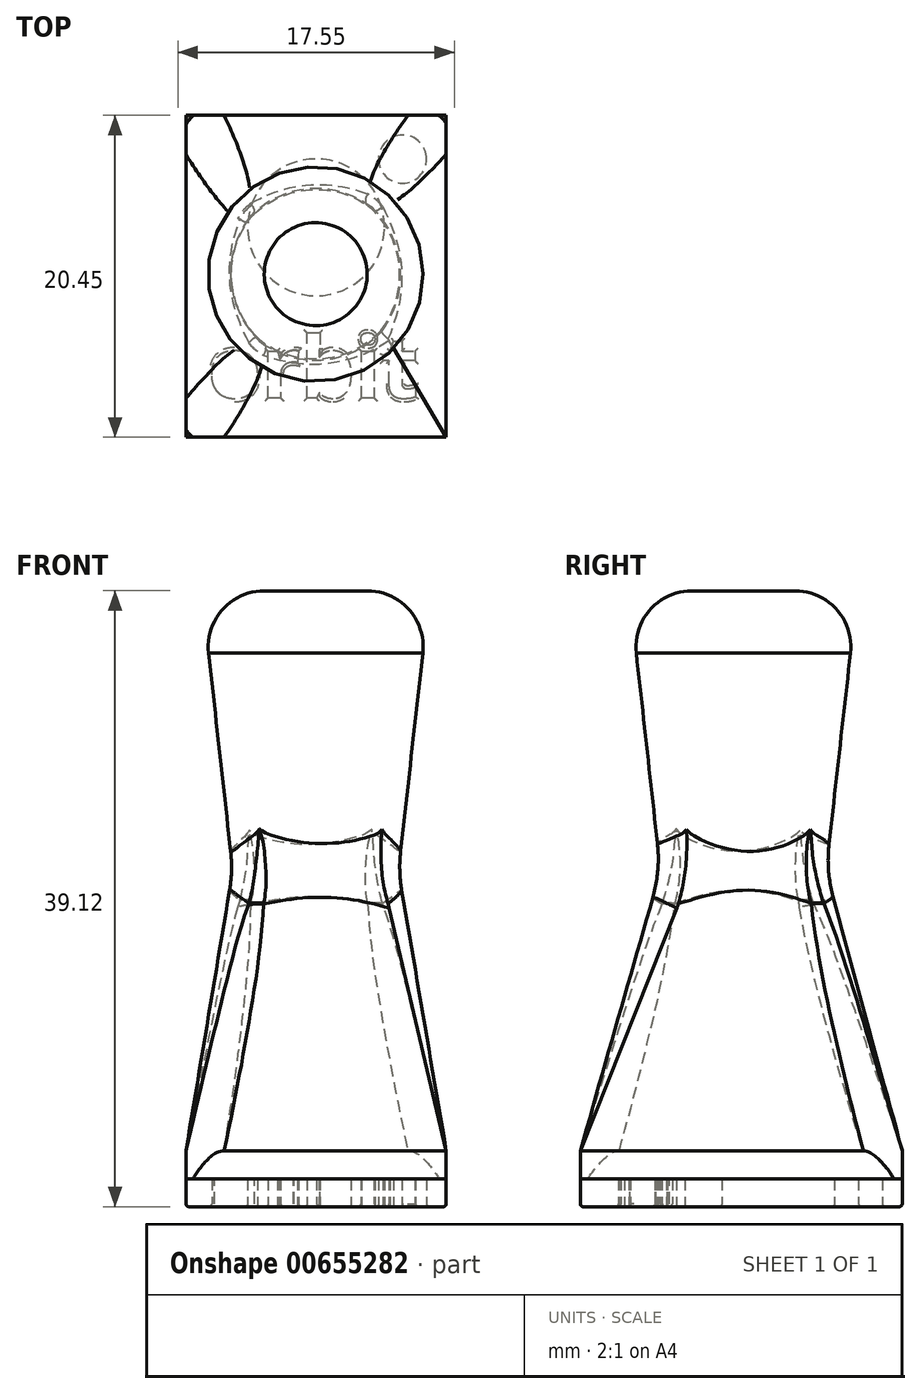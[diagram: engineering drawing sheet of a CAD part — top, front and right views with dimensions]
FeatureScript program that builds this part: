
annotation { "Feature Type Name" : "Feature", "Feature Type Description" : "" }
export const myFeature = defineFeature(function(context is Context, id is Id, definition is map)
    precondition{}
    {
        {
            var Q0;
            Q0=qCreatedBy(makeId("Top.planeOp"),FACE);
            var sketch = newSketch(context, id + "F0", { "sketchPlane" : qUnion([Q0])});
            skCircle(sketch, "E0", {"center": v(2.63, -1.24) * mm, "radius": 6.21 * mm});
            skLineSegment(sketch, "E1.bottom", {"start": v(-9.17, -20.29) * mm, "end": v(14.44, -20.29) * mm});
            skLineSegment(sketch, "E1.top", {"start": v(-9.17, 8.92) * mm, "end": v(14.44, 8.92) * mm});
            skLineSegment(sketch, "E1.left", {"start": v(-9.17, -20.29) * mm, "end": v(-9.17, 8.92) * mm});
            skLineSegment(sketch, "E1.right", {"start": v(14.44, -20.29) * mm, "end": v(14.44, 8.92) * mm});
            skPoint(sketch, "E1.middle", {"position": v(2.63, -5.68) * mm});
            skText(sketch, "E2", { "text": "orbit", "fontName": "OpenSans-Bold.ttf"});
            skCircle(sketch, "E3", {"center": v(10.48, 4.96) * mm, "radius": 2.18 * mm});
            const initialGuessF0  = {"E2": [-0.00718, -0.01673, 1, 0, 0.00562]};
            skSetInitialGuess(sketch, initialGuessF0);
            skSolve(sketch);
        }
        {
            var Q0;
            Q0=makeQuery(id+"F0.imprint","IMPRINT",FACE,{"disambiguationData":[TD([[makeQuery(id+"F0.imprint","IMPRINT",EDGE,{"derivedFrom":sQuery(id+"F0.wireOp",EDGE,"E0")}),-1.0]])]});
            var Q1;
            Q1=makeQuery(id+"F0.imprint","IMPRINT",FACE,{"disambiguationData":[TD([[makeQuery(id+"F0.imprint","IMPRINT",EDGE,{"derivedFrom":sQuery(id+"F0.wireOp",EDGE,"6c242687-06e7-4fa3-8755-0ec345e10ca5.sketch_text.stroke-45")}),1.0]])]});
            var Q2;
            Q2=makeQuery(id+"F0.imprint","IMPRINT",FACE,{"disambiguationData":[TD([[makeQuery(id+"F0.imprint","IMPRINT",EDGE,{"derivedFrom":sQuery(id+"F0.wireOp",EDGE,"6c242687-06e7-4fa3-8755-0ec345e10ca5.sketch_text.stroke-9")}),1.0]])]});
            extrude(context, id + "F1", {"entities" : qUnion([Q0, Q1, Q2]), "depth" : 2.54 * mm, "offsetDistance" : 25.4 * mm});
        }
        {
            var Q0;
            Q0=makeQuery(id+"F1.opExtrude","CAP_FACE",FACE,{"disambiguationData":[OSD([sQuery(id+"F0.wireOp",EDGE,"E0"),sQuery(id+"F0.wireOp",EDGE,"53a408db-f14d-4eee-ab72-fbaa9f21d148"),sQuery(id+"F0.wireOp",EDGE,"6c242687-06e7-4fa3-8755-0ec345e10ca5.sketch_text.stroke-0"),sQuery(id+"F0.wireOp",EDGE,"6c242687-06e7-4fa3-8755-0ec345e10ca5.sketch_text.stroke-1"),sQuery(id+"F0.wireOp",EDGE,"6c242687-06e7-4fa3-8755-0ec345e10ca5.sketch_text.stroke-2"),sQuery(id+"F0.wireOp",EDGE,"6c242687-06e7-4fa3-8755-0ec345e10ca5.sketch_text.stroke-3"),sQuery(id+"F0.wireOp",EDGE,"6c242687-06e7-4fa3-8755-0ec345e10ca5.sketch_text.stroke-4"),sQuery(id+"F0.wireOp",EDGE,"6c242687-06e7-4fa3-8755-0ec345e10ca5.sketch_text.stroke-5"),sQuery(id+"F0.wireOp",EDGE,"6c242687-06e7-4fa3-8755-0ec345e10ca5.sketch_text.stroke-6"),sQuery(id+"F0.wireOp",EDGE,"6c242687-06e7-4fa3-8755-0ec345e10ca5.sketch_text.stroke-7"),sQuery(id+"F0.wireOp",EDGE,"6c242687-06e7-4fa3-8755-0ec345e10ca5.sketch_text.stroke-8"),sQuery(id+"F0.wireOp",EDGE,"6c242687-06e7-4fa3-8755-0ec345e10ca5.sketch_text.stroke-17"),sQuery(id+"F0.wireOp",EDGE,"6c242687-06e7-4fa3-8755-0ec345e10ca5.sketch_text.stroke-18"),sQuery(id+"F0.wireOp",EDGE,"6c242687-06e7-4fa3-8755-0ec345e10ca5.sketch_text.stroke-19"),sQuery(id+"F0.wireOp",EDGE,"6c242687-06e7-4fa3-8755-0ec345e10ca5.sketch_text.stroke-20"),sQuery(id+"F0.wireOp",EDGE,"6c242687-06e7-4fa3-8755-0ec345e10ca5.sketch_text.stroke-21"),sQuery(id+"F0.wireOp",EDGE,"6c242687-06e7-4fa3-8755-0ec345e10ca5.sketch_text.stroke-22"),sQuery(id+"F0.wireOp",EDGE,"6c242687-06e7-4fa3-8755-0ec345e10ca5.sketch_text.stroke-23"),sQuery(id+"F0.wireOp",EDGE,"6c242687-06e7-4fa3-8755-0ec345e10ca5.sketch_text.stroke-24"),sQuery(id+"F0.wireOp",EDGE,"6c242687-06e7-4fa3-8755-0ec345e10ca5.sketch_text.stroke-25"),sQuery(id+"F0.wireOp",EDGE,"6c242687-06e7-4fa3-8755-0ec345e10ca5.sketch_text.stroke-26"),sQuery(id+"F0.wireOp",EDGE,"6c242687-06e7-4fa3-8755-0ec345e10ca5.sketch_text.stroke-27"),sQuery(id+"F0.wireOp",EDGE,"6c242687-06e7-4fa3-8755-0ec345e10ca5.sketch_text.stroke-28"),sQuery(id+"F0.wireOp",EDGE,"6c242687-06e7-4fa3-8755-0ec345e10ca5.sketch_text.stroke-29"),sQuery(id+"F0.wireOp",EDGE,"6c242687-06e7-4fa3-8755-0ec345e10ca5.sketch_text.stroke-30"),sQuery(id+"F0.wireOp",EDGE,"6c242687-06e7-4fa3-8755-0ec345e10ca5.sketch_text.stroke-31"),sQuery(id+"F0.wireOp",EDGE,"6c242687-06e7-4fa3-8755-0ec345e10ca5.sketch_text.stroke-32"),sQuery(id+"F0.wireOp",EDGE,"6c242687-06e7-4fa3-8755-0ec345e10ca5.sketch_text.stroke-33"),sQuery(id+"F0.wireOp",EDGE,"6c242687-06e7-4fa3-8755-0ec345e10ca5.sketch_text.stroke-34"),sQuery(id+"F0.wireOp",EDGE,"6c242687-06e7-4fa3-8755-0ec345e10ca5.sketch_text.stroke-35"),sQuery(id+"F0.wireOp",EDGE,"6c242687-06e7-4fa3-8755-0ec345e10ca5.sketch_text.stroke-36"),sQuery(id+"F0.wireOp",EDGE,"6c242687-06e7-4fa3-8755-0ec345e10ca5.sketch_text.stroke-37"),sQuery(id+"F0.wireOp",EDGE,"6c242687-06e7-4fa3-8755-0ec345e10ca5.sketch_text.stroke-38"),sQuery(id+"F0.wireOp",EDGE,"6c242687-06e7-4fa3-8755-0ec345e10ca5.sketch_text.stroke-39"),sQuery(id+"F0.wireOp",EDGE,"6c242687-06e7-4fa3-8755-0ec345e10ca5.sketch_text.stroke-40"),sQuery(id+"F0.wireOp",EDGE,"6c242687-06e7-4fa3-8755-0ec345e10ca5.sketch_text.stroke-41"),sQuery(id+"F0.wireOp",EDGE,"6c242687-06e7-4fa3-8755-0ec345e10ca5.sketch_text.stroke-42"),sQuery(id+"F0.wireOp",EDGE,"6c242687-06e7-4fa3-8755-0ec345e10ca5.sketch_text.stroke-43"),sQuery(id+"F0.wireOp",EDGE,"6c242687-06e7-4fa3-8755-0ec345e10ca5.sketch_text.stroke-44"),sQuery(id+"F0.wireOp",EDGE,"6c242687-06e7-4fa3-8755-0ec345e10ca5.sketch_text.stroke-53"),sQuery(id+"F0.wireOp",EDGE,"6c242687-06e7-4fa3-8755-0ec345e10ca5.sketch_text.stroke-54"),sQuery(id+"F0.wireOp",EDGE,"6c242687-06e7-4fa3-8755-0ec345e10ca5.sketch_text.stroke-55"),sQuery(id+"F0.wireOp",EDGE,"6c242687-06e7-4fa3-8755-0ec345e10ca5.sketch_text.stroke-56"),sQuery(id+"F0.wireOp",EDGE,"6c242687-06e7-4fa3-8755-0ec345e10ca5.sketch_text.stroke-57"),sQuery(id+"F0.wireOp",EDGE,"6c242687-06e7-4fa3-8755-0ec345e10ca5.sketch_text.stroke-58"),sQuery(id+"F0.wireOp",EDGE,"6c242687-06e7-4fa3-8755-0ec345e10ca5.sketch_text.stroke-59"),sQuery(id+"F0.wireOp",EDGE,"6c242687-06e7-4fa3-8755-0ec345e10ca5.sketch_text.stroke-60"),sQuery(id+"F0.wireOp",EDGE,"6c242687-06e7-4fa3-8755-0ec345e10ca5.sketch_text.stroke-61"),sQuery(id+"F0.wireOp",EDGE,"6c242687-06e7-4fa3-8755-0ec345e10ca5.sketch_text.stroke-62"),sQuery(id+"F0.wireOp",EDGE,"6c242687-06e7-4fa3-8755-0ec345e10ca5.sketch_text.stroke-63"),sQuery(id+"F0.wireOp",EDGE,"6c242687-06e7-4fa3-8755-0ec345e10ca5.sketch_text.stroke-64"),sQuery(id+"F0.wireOp",EDGE,"6c242687-06e7-4fa3-8755-0ec345e10ca5.sketch_text.stroke-65"),sQuery(id+"F0.wireOp",EDGE,"6c242687-06e7-4fa3-8755-0ec345e10ca5.sketch_text.stroke-66"),sQuery(id+"F0.wireOp",EDGE,"6c242687-06e7-4fa3-8755-0ec345e10ca5.sketch_text.stroke-67"),sQuery(id+"F0.wireOp",EDGE,"6c242687-06e7-4fa3-8755-0ec345e10ca5.sketch_text.stroke-68"),sQuery(id+"F0.wireOp",EDGE,"6c242687-06e7-4fa3-8755-0ec345e10ca5.sketch_text.stroke-69"),sQuery(id+"F0.wireOp",EDGE,"6c242687-06e7-4fa3-8755-0ec345e10ca5.sketch_text.stroke-70"),sQuery(id+"F0.wireOp",EDGE,"6c242687-06e7-4fa3-8755-0ec345e10ca5.sketch_text.stroke-71"),sQuery(id+"F0.wireOp",EDGE,"6c242687-06e7-4fa3-8755-0ec345e10ca5.sketch_text.stroke-72"),sQuery(id+"F0.wireOp",EDGE,"6c242687-06e7-4fa3-8755-0ec345e10ca5.sketch_text.stroke-73"),sQuery(id+"F0.wireOp",EDGE,"6c242687-06e7-4fa3-8755-0ec345e10ca5.sketch_text.stroke-74"),sQuery(id+"F0.wireOp",EDGE,"6c242687-06e7-4fa3-8755-0ec345e10ca5.sketch_text.stroke-75"),sQuery(id+"F0.wireOp",EDGE,"6c242687-06e7-4fa3-8755-0ec345e10ca5.sketch_text.stroke-76"),sQuery(id+"F0.wireOp",EDGE,"6c242687-06e7-4fa3-8755-0ec345e10ca5.sketch_text.stroke-77"),sQuery(id+"F0.wireOp",EDGE,"6c242687-06e7-4fa3-8755-0ec345e10ca5.sketch_text.stroke-78"),sQuery(id+"F0.wireOp",EDGE,"6c242687-06e7-4fa3-8755-0ec345e10ca5.sketch_text.stroke-79"),sQuery(id+"F0.wireOp",EDGE,"6c242687-06e7-4fa3-8755-0ec345e10ca5.sketch_text.stroke-80"),sQuery(id+"F0.wireOp",EDGE,"6c242687-06e7-4fa3-8755-0ec345e10ca5.sketch_text.stroke-81"),sQuery(id+"F0.wireOp",EDGE,"6c242687-06e7-4fa3-8755-0ec345e10ca5.sketch_text.stroke-82"),sQuery(id+"F0.wireOp",EDGE,"6c242687-06e7-4fa3-8755-0ec345e10ca5.sketch_text.stroke-83"),sQuery(id+"F0.wireOp",EDGE,"E1.bottom"),sQuery(id+"F0.wireOp",EDGE,"E1.top"),sQuery(id+"F0.wireOp",EDGE,"E1.left"),sQuery(id+"F0.wireOp",EDGE,"E1.right")])],"isStart":false});
            var sketch = newSketch(context, id + "F2", { "sketchPlane" : qUnion([Q0])});
            skLineSegment(sketch, "E4.bottom", {"start": v(14.44, -20.29) * mm, "end": v(-9.17, -20.29) * mm});
            skLineSegment(sketch, "E4.top", {"start": v(14.44, 8.92) * mm, "end": v(-9.17, 8.92) * mm});
            skLineSegment(sketch, "E4.left", {"start": v(14.44, -20.29) * mm, "end": v(14.44, 8.92) * mm});
            skLineSegment(sketch, "E4.right", {"start": v(-9.17, -20.29) * mm, "end": v(-9.17, 8.92) * mm});
            skSolve(sketch);
        }
        {
            var Q0;
            Q0 = qSketchRegion(id + "F2", true);
            extrude(context, id + "F3", {"entities" : qUnion([Q0]), "depth" : 2.54 * mm, "offsetDistance" : 25.4 * mm});
        }
        {
            var Q0;
            Q0=makeQuery(id+"F1.opExtrude","CAP_EDGE",EDGE,{"disambiguationData":[OSD([sQuery(id+"F0.wireOp",EDGE,"E0")])],"isStart":true});
            var Q1;
            Q1=makeQuery(id+"F1.opExtrude","CAP_EDGE",EDGE,{"disambiguationData":[OSD([sQuery(id+"F0.wireOp",EDGE,"53a408db-f14d-4eee-ab72-fbaa9f21d148")])],"isStart":true});
            fillet(context, id + "F4", {"entities" : qUnion([Q0, Q1]), "radius" : 0.25 * mm, "tangentPropagation" : true, "allowEdgeOverflow" : false});
        }
        {
            var Q0;
            Q0=makeQuery(id+"F1.opExtrude","CAP_FACE",FACE,{"disambiguationData":[OSD([sQuery(id+"F0.wireOp",EDGE,"E0"),sQuery(id+"F0.wireOp",EDGE,"53a408db-f14d-4eee-ab72-fbaa9f21d148"),sQuery(id+"F0.wireOp",EDGE,"6c242687-06e7-4fa3-8755-0ec345e10ca5.sketch_text.stroke-0"),sQuery(id+"F0.wireOp",EDGE,"6c242687-06e7-4fa3-8755-0ec345e10ca5.sketch_text.stroke-1"),sQuery(id+"F0.wireOp",EDGE,"6c242687-06e7-4fa3-8755-0ec345e10ca5.sketch_text.stroke-2"),sQuery(id+"F0.wireOp",EDGE,"6c242687-06e7-4fa3-8755-0ec345e10ca5.sketch_text.stroke-3"),sQuery(id+"F0.wireOp",EDGE,"6c242687-06e7-4fa3-8755-0ec345e10ca5.sketch_text.stroke-4"),sQuery(id+"F0.wireOp",EDGE,"6c242687-06e7-4fa3-8755-0ec345e10ca5.sketch_text.stroke-5"),sQuery(id+"F0.wireOp",EDGE,"6c242687-06e7-4fa3-8755-0ec345e10ca5.sketch_text.stroke-6"),sQuery(id+"F0.wireOp",EDGE,"6c242687-06e7-4fa3-8755-0ec345e10ca5.sketch_text.stroke-7"),sQuery(id+"F0.wireOp",EDGE,"6c242687-06e7-4fa3-8755-0ec345e10ca5.sketch_text.stroke-8"),sQuery(id+"F0.wireOp",EDGE,"6c242687-06e7-4fa3-8755-0ec345e10ca5.sketch_text.stroke-17"),sQuery(id+"F0.wireOp",EDGE,"6c242687-06e7-4fa3-8755-0ec345e10ca5.sketch_text.stroke-18"),sQuery(id+"F0.wireOp",EDGE,"6c242687-06e7-4fa3-8755-0ec345e10ca5.sketch_text.stroke-19"),sQuery(id+"F0.wireOp",EDGE,"6c242687-06e7-4fa3-8755-0ec345e10ca5.sketch_text.stroke-20"),sQuery(id+"F0.wireOp",EDGE,"6c242687-06e7-4fa3-8755-0ec345e10ca5.sketch_text.stroke-21"),sQuery(id+"F0.wireOp",EDGE,"6c242687-06e7-4fa3-8755-0ec345e10ca5.sketch_text.stroke-22"),sQuery(id+"F0.wireOp",EDGE,"6c242687-06e7-4fa3-8755-0ec345e10ca5.sketch_text.stroke-23"),sQuery(id+"F0.wireOp",EDGE,"6c242687-06e7-4fa3-8755-0ec345e10ca5.sketch_text.stroke-24"),sQuery(id+"F0.wireOp",EDGE,"6c242687-06e7-4fa3-8755-0ec345e10ca5.sketch_text.stroke-25"),sQuery(id+"F0.wireOp",EDGE,"6c242687-06e7-4fa3-8755-0ec345e10ca5.sketch_text.stroke-26"),sQuery(id+"F0.wireOp",EDGE,"6c242687-06e7-4fa3-8755-0ec345e10ca5.sketch_text.stroke-27"),sQuery(id+"F0.wireOp",EDGE,"6c242687-06e7-4fa3-8755-0ec345e10ca5.sketch_text.stroke-28"),sQuery(id+"F0.wireOp",EDGE,"6c242687-06e7-4fa3-8755-0ec345e10ca5.sketch_text.stroke-29"),sQuery(id+"F0.wireOp",EDGE,"6c242687-06e7-4fa3-8755-0ec345e10ca5.sketch_text.stroke-30"),sQuery(id+"F0.wireOp",EDGE,"6c242687-06e7-4fa3-8755-0ec345e10ca5.sketch_text.stroke-31"),sQuery(id+"F0.wireOp",EDGE,"6c242687-06e7-4fa3-8755-0ec345e10ca5.sketch_text.stroke-32"),sQuery(id+"F0.wireOp",EDGE,"6c242687-06e7-4fa3-8755-0ec345e10ca5.sketch_text.stroke-33"),sQuery(id+"F0.wireOp",EDGE,"6c242687-06e7-4fa3-8755-0ec345e10ca5.sketch_text.stroke-34"),sQuery(id+"F0.wireOp",EDGE,"6c242687-06e7-4fa3-8755-0ec345e10ca5.sketch_text.stroke-35"),sQuery(id+"F0.wireOp",EDGE,"6c242687-06e7-4fa3-8755-0ec345e10ca5.sketch_text.stroke-36"),sQuery(id+"F0.wireOp",EDGE,"6c242687-06e7-4fa3-8755-0ec345e10ca5.sketch_text.stroke-37"),sQuery(id+"F0.wireOp",EDGE,"6c242687-06e7-4fa3-8755-0ec345e10ca5.sketch_text.stroke-38"),sQuery(id+"F0.wireOp",EDGE,"6c242687-06e7-4fa3-8755-0ec345e10ca5.sketch_text.stroke-39"),sQuery(id+"F0.wireOp",EDGE,"6c242687-06e7-4fa3-8755-0ec345e10ca5.sketch_text.stroke-40"),sQuery(id+"F0.wireOp",EDGE,"6c242687-06e7-4fa3-8755-0ec345e10ca5.sketch_text.stroke-41"),sQuery(id+"F0.wireOp",EDGE,"6c242687-06e7-4fa3-8755-0ec345e10ca5.sketch_text.stroke-42"),sQuery(id+"F0.wireOp",EDGE,"6c242687-06e7-4fa3-8755-0ec345e10ca5.sketch_text.stroke-43"),sQuery(id+"F0.wireOp",EDGE,"6c242687-06e7-4fa3-8755-0ec345e10ca5.sketch_text.stroke-44"),sQuery(id+"F0.wireOp",EDGE,"6c242687-06e7-4fa3-8755-0ec345e10ca5.sketch_text.stroke-53"),sQuery(id+"F0.wireOp",EDGE,"6c242687-06e7-4fa3-8755-0ec345e10ca5.sketch_text.stroke-54"),sQuery(id+"F0.wireOp",EDGE,"6c242687-06e7-4fa3-8755-0ec345e10ca5.sketch_text.stroke-55"),sQuery(id+"F0.wireOp",EDGE,"6c242687-06e7-4fa3-8755-0ec345e10ca5.sketch_text.stroke-56"),sQuery(id+"F0.wireOp",EDGE,"6c242687-06e7-4fa3-8755-0ec345e10ca5.sketch_text.stroke-57"),sQuery(id+"F0.wireOp",EDGE,"6c242687-06e7-4fa3-8755-0ec345e10ca5.sketch_text.stroke-58"),sQuery(id+"F0.wireOp",EDGE,"6c242687-06e7-4fa3-8755-0ec345e10ca5.sketch_text.stroke-59"),sQuery(id+"F0.wireOp",EDGE,"6c242687-06e7-4fa3-8755-0ec345e10ca5.sketch_text.stroke-60"),sQuery(id+"F0.wireOp",EDGE,"6c242687-06e7-4fa3-8755-0ec345e10ca5.sketch_text.stroke-61"),sQuery(id+"F0.wireOp",EDGE,"6c242687-06e7-4fa3-8755-0ec345e10ca5.sketch_text.stroke-62"),sQuery(id+"F0.wireOp",EDGE,"6c242687-06e7-4fa3-8755-0ec345e10ca5.sketch_text.stroke-63"),sQuery(id+"F0.wireOp",EDGE,"6c242687-06e7-4fa3-8755-0ec345e10ca5.sketch_text.stroke-64"),sQuery(id+"F0.wireOp",EDGE,"6c242687-06e7-4fa3-8755-0ec345e10ca5.sketch_text.stroke-65"),sQuery(id+"F0.wireOp",EDGE,"6c242687-06e7-4fa3-8755-0ec345e10ca5.sketch_text.stroke-66"),sQuery(id+"F0.wireOp",EDGE,"6c242687-06e7-4fa3-8755-0ec345e10ca5.sketch_text.stroke-67"),sQuery(id+"F0.wireOp",EDGE,"6c242687-06e7-4fa3-8755-0ec345e10ca5.sketch_text.stroke-68"),sQuery(id+"F0.wireOp",EDGE,"6c242687-06e7-4fa3-8755-0ec345e10ca5.sketch_text.stroke-69"),sQuery(id+"F0.wireOp",EDGE,"6c242687-06e7-4fa3-8755-0ec345e10ca5.sketch_text.stroke-70"),sQuery(id+"F0.wireOp",EDGE,"6c242687-06e7-4fa3-8755-0ec345e10ca5.sketch_text.stroke-71"),sQuery(id+"F0.wireOp",EDGE,"6c242687-06e7-4fa3-8755-0ec345e10ca5.sketch_text.stroke-72"),sQuery(id+"F0.wireOp",EDGE,"6c242687-06e7-4fa3-8755-0ec345e10ca5.sketch_text.stroke-73"),sQuery(id+"F0.wireOp",EDGE,"6c242687-06e7-4fa3-8755-0ec345e10ca5.sketch_text.stroke-74"),sQuery(id+"F0.wireOp",EDGE,"6c242687-06e7-4fa3-8755-0ec345e10ca5.sketch_text.stroke-75"),sQuery(id+"F0.wireOp",EDGE,"6c242687-06e7-4fa3-8755-0ec345e10ca5.sketch_text.stroke-76"),sQuery(id+"F0.wireOp",EDGE,"6c242687-06e7-4fa3-8755-0ec345e10ca5.sketch_text.stroke-77"),sQuery(id+"F0.wireOp",EDGE,"6c242687-06e7-4fa3-8755-0ec345e10ca5.sketch_text.stroke-78"),sQuery(id+"F0.wireOp",EDGE,"6c242687-06e7-4fa3-8755-0ec345e10ca5.sketch_text.stroke-79"),sQuery(id+"F0.wireOp",EDGE,"6c242687-06e7-4fa3-8755-0ec345e10ca5.sketch_text.stroke-80"),sQuery(id+"F0.wireOp",EDGE,"6c242687-06e7-4fa3-8755-0ec345e10ca5.sketch_text.stroke-81"),sQuery(id+"F0.wireOp",EDGE,"6c242687-06e7-4fa3-8755-0ec345e10ca5.sketch_text.stroke-82"),sQuery(id+"F0.wireOp",EDGE,"6c242687-06e7-4fa3-8755-0ec345e10ca5.sketch_text.stroke-83"),sQuery(id+"F0.wireOp",EDGE,"E1.bottom"),sQuery(id+"F0.wireOp",EDGE,"E1.top"),sQuery(id+"F0.wireOp",EDGE,"E1.left"),sQuery(id+"F0.wireOp",EDGE,"E1.right")])],"isStart":true});
            var Q1;
            Q1=makeQuery(id+"F1.opExtrude","CAP_FACE",FACE,{"disambiguationData":[OSD([sQuery(id+"F0.wireOp",EDGE,"6c242687-06e7-4fa3-8755-0ec345e10ca5.sketch_text.stroke-45"),sQuery(id+"F0.wireOp",EDGE,"6c242687-06e7-4fa3-8755-0ec345e10ca5.sketch_text.stroke-46"),sQuery(id+"F0.wireOp",EDGE,"6c242687-06e7-4fa3-8755-0ec345e10ca5.sketch_text.stroke-47"),sQuery(id+"F0.wireOp",EDGE,"6c242687-06e7-4fa3-8755-0ec345e10ca5.sketch_text.stroke-48"),sQuery(id+"F0.wireOp",EDGE,"6c242687-06e7-4fa3-8755-0ec345e10ca5.sketch_text.stroke-49"),sQuery(id+"F0.wireOp",EDGE,"6c242687-06e7-4fa3-8755-0ec345e10ca5.sketch_text.stroke-50"),sQuery(id+"F0.wireOp",EDGE,"6c242687-06e7-4fa3-8755-0ec345e10ca5.sketch_text.stroke-51"),sQuery(id+"F0.wireOp",EDGE,"6c242687-06e7-4fa3-8755-0ec345e10ca5.sketch_text.stroke-52")])],"isStart":true});
            var Q2;
            Q2=makeQuery(id+"F1.opExtrude","CAP_FACE",FACE,{"disambiguationData":[OSD([sQuery(id+"F0.wireOp",EDGE,"6c242687-06e7-4fa3-8755-0ec345e10ca5.sketch_text.stroke-9"),sQuery(id+"F0.wireOp",EDGE,"6c242687-06e7-4fa3-8755-0ec345e10ca5.sketch_text.stroke-10"),sQuery(id+"F0.wireOp",EDGE,"6c242687-06e7-4fa3-8755-0ec345e10ca5.sketch_text.stroke-11"),sQuery(id+"F0.wireOp",EDGE,"6c242687-06e7-4fa3-8755-0ec345e10ca5.sketch_text.stroke-12"),sQuery(id+"F0.wireOp",EDGE,"6c242687-06e7-4fa3-8755-0ec345e10ca5.sketch_text.stroke-13"),sQuery(id+"F0.wireOp",EDGE,"6c242687-06e7-4fa3-8755-0ec345e10ca5.sketch_text.stroke-14"),sQuery(id+"F0.wireOp",EDGE,"6c242687-06e7-4fa3-8755-0ec345e10ca5.sketch_text.stroke-15"),sQuery(id+"F0.wireOp",EDGE,"6c242687-06e7-4fa3-8755-0ec345e10ca5.sketch_text.stroke-16")])],"isStart":true});
            fillet(context, id + "F5", {"entities" : qUnion([Q0, Q1, Q2]), "radius" : 0.25 * mm, "tangentPropagation" : true, "allowEdgeOverflow" : false});
        }
        {
            var Q0;
            Q0=makeQuery(id+"F3.opExtrude","CAP_FACE",FACE,{"disambiguationData":[OSD([sQuery(id+"F2.wireOp",EDGE,"E4.bottom"),sQuery(id+"F2.wireOp",EDGE,"E4.top"),sQuery(id+"F2.wireOp",EDGE,"E4.left"),sQuery(id+"F2.wireOp",EDGE,"E4.right")])],"isStart":false});
            cPlane(context, id + "F6", {"entities" : qUnion([Q0]), "cplaneType" : CPlaneType.OFFSET, "offset" : 25.4 * mm, "width" : 152.4 * mm, "height" : 152.4 * mm});
        }
        {
            var Q0;
            Q0=qCreatedBy(id+"F6.planeOp",FACE);
            var sketch = newSketch(context, id + "F7", { "sketchPlane" : qUnion([Q0])});
            skCircle(sketch, "E5", {"center": v(2.59, -5.5) * mm, "radius": 7.51 * mm});
            skSolve(sketch);
        }
        {
            var Q1;
            Q1=makeQuery(id+"F3.opExtrude","CAP_FACE",FACE,{"disambiguationData":[OSD([sQuery(id+"F2.wireOp",EDGE,"E4.bottom"),sQuery(id+"F2.wireOp",EDGE,"E4.top"),sQuery(id+"F2.wireOp",EDGE,"E4.left"),sQuery(id+"F2.wireOp",EDGE,"E4.right")])],"isStart":false});
            var Q2;
            Q2=makeQuery(id+"F7.imprint","IMPRINT",FACE,{"disambiguationData":[TD([[makeQuery(id+"F7.imprint","IMPRINT",EDGE,{"derivedFrom":sQuery(id+"F7.wireOp",EDGE,"E5")}),1.0]])]});
            loft(context, id + "F8", {"operationType" : NewBodyOperationType.ADD, "sheetProfilesArray" : [{ "sheetProfileEntities" : qUnion([Q1]) }, { "sheetProfileEntities" : qUnion([Q2]) }]});
        }
        {
            var Q0;
            Q0=makeQuery(id+"F8.opLoft","CAP_FACE",FACE,{"disambiguationData":[OSD([makeQuery(id+"F7.imprint","IMPRINT",FACE,{"disambiguationData":[TD([[makeQuery(id+"F7.imprint","IMPRINT",EDGE,{"derivedFrom":sQuery(id+"F7.wireOp",EDGE,"E5")}),1.0]])]})])],"isStart":true});
            cPlane(context, id + "F9", {"entities" : qUnion([Q0]), "cplaneType" : CPlaneType.OFFSET, "offset" : 25.4 * mm, "width" : 152.4 * mm, "height" : 152.4 * mm});
        }
        {
            var Q0;
            Q0=qCreatedBy(id+"F9.planeOp",FACE);
            var sketch = newSketch(context, id + "F10", { "sketchPlane" : qUnion([Q0])});
            skCircle(sketch, "E6", {"center": v(2.6, -5.48) * mm, "radius": 10.35 * mm});
            skSolve(sketch);
        }
        {
            var Q1;
            Q1=makeQuery(id+"F8.opLoft","CAP_FACE",FACE,{"disambiguationData":[OSD([makeQuery(id+"F7.imprint","IMPRINT",FACE,{"disambiguationData":[TD([[makeQuery(id+"F7.imprint","IMPRINT",EDGE,{"derivedFrom":sQuery(id+"F7.wireOp",EDGE,"E5")}),1.0]])]})])],"isStart":true});
            var Q2;
            Q2=makeQuery(id+"F10.imprint","IMPRINT",FACE,{"disambiguationData":[TD([[makeQuery(id+"F10.imprint","IMPRINT",EDGE,{"derivedFrom":sQuery(id+"F10.wireOp",EDGE,"E6")}),1.0]])]});
            loft(context, id + "F11", {"operationType" : NewBodyOperationType.ADD, "sheetProfilesArray" : [{ "sheetProfileEntities" : qUnion([Q1]) }, { "sheetProfileEntities" : qUnion([Q2]) }]});
        }
        {
            var Q0;
            {var subQ0=sQuery(id+"F7.wireOp",EDGE,"E5");var subQ1=sQuery(id+"F2.wireOp",EDGE,"E4.right");var subQ2=sQuery(id+"F2.wireOp",EDGE,"E4.bottom");Q0=makeQuery(id+"F11.boolean.opBoolean","MERGE",EDGE,{"derivedFrom":[makeQuery(id+"F8.opLoft","MID_CAP_EDGE",EDGE,{"disambiguationData":[OSD([subQ2,subQ1,subQ0])],"capPos":1.0}),makeQuery(id+"F11.opLoft","MID_CAP_EDGE",EDGE,{"disambiguationData":[OSD([subQ2,subQ1,subQ0])],"capPos":0.0})]});}
            var Q1;
            {var subQ0=sQuery(id+"F7.wireOp",EDGE,"E5");var subQ1=sQuery(id+"F2.wireOp",EDGE,"E4.right");var subQ2=sQuery(id+"F2.wireOp",EDGE,"E4.left");var subQ3=sQuery(id+"F2.wireOp",EDGE,"E4.top");var subQ4=sQuery(id+"F2.wireOp",EDGE,"E4.bottom");Q1=makeQuery(id+"F11.boolean.opBoolean","MERGE",EDGE,{"derivedFrom":[makeQuery(id+"F8.opLoft","MID_CAP_EDGE",EDGE,{"disambiguationData":[OSD([subQ4,subQ3,subQ2,subQ1,subQ0])],"capPos":1.0}),makeQuery(id+"F11.opLoft","MID_CAP_EDGE",EDGE,{"disambiguationData":[OSD([subQ4,subQ3,subQ2,subQ1,subQ0])],"capPos":0.0})]});}
            var Q2;
            {var subQ0=sQuery(id+"F7.wireOp",EDGE,"E5");var subQ1=sQuery(id+"F2.wireOp",EDGE,"E4.left");var subQ2=sQuery(id+"F2.wireOp",EDGE,"E4.top");var subQ3=sQuery(id+"F2.wireOp",EDGE,"E4.bottom");Q2=makeQuery(id+"F11.boolean.opBoolean","MERGE",EDGE,{"derivedFrom":[makeQuery(id+"F8.opLoft","MID_CAP_EDGE",EDGE,{"disambiguationData":[OSD([subQ3,subQ2,subQ1,subQ0])],"capPos":1.0}),makeQuery(id+"F11.opLoft","MID_CAP_EDGE",EDGE,{"disambiguationData":[OSD([subQ3,subQ2,subQ1,subQ0])],"capPos":0.0})]});}
            var Q3;
            {var subQ0=sQuery(id+"F7.wireOp",EDGE,"E5");var subQ1=sQuery(id+"F2.wireOp",EDGE,"E4.right");var subQ2=sQuery(id+"F2.wireOp",EDGE,"E4.left");var subQ3=sQuery(id+"F2.wireOp",EDGE,"E4.bottom");Q3=makeQuery(id+"F11.boolean.opBoolean","MERGE",EDGE,{"derivedFrom":[makeQuery(id+"F8.opLoft","MID_CAP_EDGE",EDGE,{"disambiguationData":[OSD([subQ3,subQ2,subQ1,subQ0])],"capPos":1.0}),makeQuery(id+"F11.opLoft","MID_CAP_EDGE",EDGE,{"disambiguationData":[OSD([subQ3,subQ2,subQ1,subQ0])],"capPos":0.0})]});}
            fillet(context, id + "F12", {"entities" : qUnion([Q0, Q1, Q2, Q3]), "radius" : 12.7 * mm, "tangentPropagation" : true, "allowEdgeOverflow" : false});
        }
        {
            var Q0;
            Q0=makeQuery(id+"F11.opLoft","CAP_FACE",FACE,{"disambiguationData":[OSD([makeQuery(id+"F10.imprint","IMPRINT",FACE,{"disambiguationData":[TD([[makeQuery(id+"F10.imprint","IMPRINT",EDGE,{"derivedFrom":sQuery(id+"F10.wireOp",EDGE,"E6")}),1.0]])]})])],"isStart":true});
            fillet(context, id + "F13", {"entities" : qUnion([Q0]), "radius" : 5.08 * mm, "tangentPropagation" : true, "allowEdgeOverflow" : false});
        }
        {
            var Q0;
            Q0=makeQuery(id+"F1.opExtrude","SWEPT_BODY",BODY,{"disambiguationData":[OSD([sQuery(id+"F0.wireOp",EDGE,"E0"),sQuery(id+"F0.wireOp",EDGE,"53a408db-f14d-4eee-ab72-fbaa9f21d148"),sQuery(id+"F0.wireOp",EDGE,"6c242687-06e7-4fa3-8755-0ec345e10ca5.sketch_text.stroke-0"),sQuery(id+"F0.wireOp",EDGE,"6c242687-06e7-4fa3-8755-0ec345e10ca5.sketch_text.stroke-1"),sQuery(id+"F0.wireOp",EDGE,"6c242687-06e7-4fa3-8755-0ec345e10ca5.sketch_text.stroke-2"),sQuery(id+"F0.wireOp",EDGE,"6c242687-06e7-4fa3-8755-0ec345e10ca5.sketch_text.stroke-3"),sQuery(id+"F0.wireOp",EDGE,"6c242687-06e7-4fa3-8755-0ec345e10ca5.sketch_text.stroke-4"),sQuery(id+"F0.wireOp",EDGE,"6c242687-06e7-4fa3-8755-0ec345e10ca5.sketch_text.stroke-5"),sQuery(id+"F0.wireOp",EDGE,"6c242687-06e7-4fa3-8755-0ec345e10ca5.sketch_text.stroke-6"),sQuery(id+"F0.wireOp",EDGE,"6c242687-06e7-4fa3-8755-0ec345e10ca5.sketch_text.stroke-7"),sQuery(id+"F0.wireOp",EDGE,"6c242687-06e7-4fa3-8755-0ec345e10ca5.sketch_text.stroke-8"),sQuery(id+"F0.wireOp",EDGE,"6c242687-06e7-4fa3-8755-0ec345e10ca5.sketch_text.stroke-17"),sQuery(id+"F0.wireOp",EDGE,"6c242687-06e7-4fa3-8755-0ec345e10ca5.sketch_text.stroke-18"),sQuery(id+"F0.wireOp",EDGE,"6c242687-06e7-4fa3-8755-0ec345e10ca5.sketch_text.stroke-19"),sQuery(id+"F0.wireOp",EDGE,"6c242687-06e7-4fa3-8755-0ec345e10ca5.sketch_text.stroke-20"),sQuery(id+"F0.wireOp",EDGE,"6c242687-06e7-4fa3-8755-0ec345e10ca5.sketch_text.stroke-21"),sQuery(id+"F0.wireOp",EDGE,"6c242687-06e7-4fa3-8755-0ec345e10ca5.sketch_text.stroke-22"),sQuery(id+"F0.wireOp",EDGE,"6c242687-06e7-4fa3-8755-0ec345e10ca5.sketch_text.stroke-23"),sQuery(id+"F0.wireOp",EDGE,"6c242687-06e7-4fa3-8755-0ec345e10ca5.sketch_text.stroke-24"),sQuery(id+"F0.wireOp",EDGE,"6c242687-06e7-4fa3-8755-0ec345e10ca5.sketch_text.stroke-25"),sQuery(id+"F0.wireOp",EDGE,"6c242687-06e7-4fa3-8755-0ec345e10ca5.sketch_text.stroke-26"),sQuery(id+"F0.wireOp",EDGE,"6c242687-06e7-4fa3-8755-0ec345e10ca5.sketch_text.stroke-27"),sQuery(id+"F0.wireOp",EDGE,"6c242687-06e7-4fa3-8755-0ec345e10ca5.sketch_text.stroke-28"),sQuery(id+"F0.wireOp",EDGE,"6c242687-06e7-4fa3-8755-0ec345e10ca5.sketch_text.stroke-29"),sQuery(id+"F0.wireOp",EDGE,"6c242687-06e7-4fa3-8755-0ec345e10ca5.sketch_text.stroke-30"),sQuery(id+"F0.wireOp",EDGE,"6c242687-06e7-4fa3-8755-0ec345e10ca5.sketch_text.stroke-31"),sQuery(id+"F0.wireOp",EDGE,"6c242687-06e7-4fa3-8755-0ec345e10ca5.sketch_text.stroke-32"),sQuery(id+"F0.wireOp",EDGE,"6c242687-06e7-4fa3-8755-0ec345e10ca5.sketch_text.stroke-33"),sQuery(id+"F0.wireOp",EDGE,"6c242687-06e7-4fa3-8755-0ec345e10ca5.sketch_text.stroke-34"),sQuery(id+"F0.wireOp",EDGE,"6c242687-06e7-4fa3-8755-0ec345e10ca5.sketch_text.stroke-35"),sQuery(id+"F0.wireOp",EDGE,"6c242687-06e7-4fa3-8755-0ec345e10ca5.sketch_text.stroke-36"),sQuery(id+"F0.wireOp",EDGE,"6c242687-06e7-4fa3-8755-0ec345e10ca5.sketch_text.stroke-37"),sQuery(id+"F0.wireOp",EDGE,"6c242687-06e7-4fa3-8755-0ec345e10ca5.sketch_text.stroke-38"),sQuery(id+"F0.wireOp",EDGE,"6c242687-06e7-4fa3-8755-0ec345e10ca5.sketch_text.stroke-39"),sQuery(id+"F0.wireOp",EDGE,"6c242687-06e7-4fa3-8755-0ec345e10ca5.sketch_text.stroke-40"),sQuery(id+"F0.wireOp",EDGE,"6c242687-06e7-4fa3-8755-0ec345e10ca5.sketch_text.stroke-41"),sQuery(id+"F0.wireOp",EDGE,"6c242687-06e7-4fa3-8755-0ec345e10ca5.sketch_text.stroke-42"),sQuery(id+"F0.wireOp",EDGE,"6c242687-06e7-4fa3-8755-0ec345e10ca5.sketch_text.stroke-43"),sQuery(id+"F0.wireOp",EDGE,"6c242687-06e7-4fa3-8755-0ec345e10ca5.sketch_text.stroke-44"),sQuery(id+"F0.wireOp",EDGE,"6c242687-06e7-4fa3-8755-0ec345e10ca5.sketch_text.stroke-53"),sQuery(id+"F0.wireOp",EDGE,"6c242687-06e7-4fa3-8755-0ec345e10ca5.sketch_text.stroke-54"),sQuery(id+"F0.wireOp",EDGE,"6c242687-06e7-4fa3-8755-0ec345e10ca5.sketch_text.stroke-55"),sQuery(id+"F0.wireOp",EDGE,"6c242687-06e7-4fa3-8755-0ec345e10ca5.sketch_text.stroke-56"),sQuery(id+"F0.wireOp",EDGE,"6c242687-06e7-4fa3-8755-0ec345e10ca5.sketch_text.stroke-57"),sQuery(id+"F0.wireOp",EDGE,"6c242687-06e7-4fa3-8755-0ec345e10ca5.sketch_text.stroke-58"),sQuery(id+"F0.wireOp",EDGE,"6c242687-06e7-4fa3-8755-0ec345e10ca5.sketch_text.stroke-59"),sQuery(id+"F0.wireOp",EDGE,"6c242687-06e7-4fa3-8755-0ec345e10ca5.sketch_text.stroke-60"),sQuery(id+"F0.wireOp",EDGE,"6c242687-06e7-4fa3-8755-0ec345e10ca5.sketch_text.stroke-61"),sQuery(id+"F0.wireOp",EDGE,"6c242687-06e7-4fa3-8755-0ec345e10ca5.sketch_text.stroke-62"),sQuery(id+"F0.wireOp",EDGE,"6c242687-06e7-4fa3-8755-0ec345e10ca5.sketch_text.stroke-63"),sQuery(id+"F0.wireOp",EDGE,"6c242687-06e7-4fa3-8755-0ec345e10ca5.sketch_text.stroke-64"),sQuery(id+"F0.wireOp",EDGE,"6c242687-06e7-4fa3-8755-0ec345e10ca5.sketch_text.stroke-65"),sQuery(id+"F0.wireOp",EDGE,"6c242687-06e7-4fa3-8755-0ec345e10ca5.sketch_text.stroke-66"),sQuery(id+"F0.wireOp",EDGE,"6c242687-06e7-4fa3-8755-0ec345e10ca5.sketch_text.stroke-67"),sQuery(id+"F0.wireOp",EDGE,"6c242687-06e7-4fa3-8755-0ec345e10ca5.sketch_text.stroke-68"),sQuery(id+"F0.wireOp",EDGE,"6c242687-06e7-4fa3-8755-0ec345e10ca5.sketch_text.stroke-69"),sQuery(id+"F0.wireOp",EDGE,"6c242687-06e7-4fa3-8755-0ec345e10ca5.sketch_text.stroke-70"),sQuery(id+"F0.wireOp",EDGE,"6c242687-06e7-4fa3-8755-0ec345e10ca5.sketch_text.stroke-71"),sQuery(id+"F0.wireOp",EDGE,"6c242687-06e7-4fa3-8755-0ec345e10ca5.sketch_text.stroke-72"),sQuery(id+"F0.wireOp",EDGE,"6c242687-06e7-4fa3-8755-0ec345e10ca5.sketch_text.stroke-73"),sQuery(id+"F0.wireOp",EDGE,"6c242687-06e7-4fa3-8755-0ec345e10ca5.sketch_text.stroke-74"),sQuery(id+"F0.wireOp",EDGE,"6c242687-06e7-4fa3-8755-0ec345e10ca5.sketch_text.stroke-75"),sQuery(id+"F0.wireOp",EDGE,"6c242687-06e7-4fa3-8755-0ec345e10ca5.sketch_text.stroke-76"),sQuery(id+"F0.wireOp",EDGE,"6c242687-06e7-4fa3-8755-0ec345e10ca5.sketch_text.stroke-77"),sQuery(id+"F0.wireOp",EDGE,"6c242687-06e7-4fa3-8755-0ec345e10ca5.sketch_text.stroke-78"),sQuery(id+"F0.wireOp",EDGE,"6c242687-06e7-4fa3-8755-0ec345e10ca5.sketch_text.stroke-79"),sQuery(id+"F0.wireOp",EDGE,"6c242687-06e7-4fa3-8755-0ec345e10ca5.sketch_text.stroke-80"),sQuery(id+"F0.wireOp",EDGE,"6c242687-06e7-4fa3-8755-0ec345e10ca5.sketch_text.stroke-81"),sQuery(id+"F0.wireOp",EDGE,"6c242687-06e7-4fa3-8755-0ec345e10ca5.sketch_text.stroke-82"),sQuery(id+"F0.wireOp",EDGE,"6c242687-06e7-4fa3-8755-0ec345e10ca5.sketch_text.stroke-83"),sQuery(id+"F0.wireOp",EDGE,"E1.bottom"),sQuery(id+"F0.wireOp",EDGE,"E1.top"),sQuery(id+"F0.wireOp",EDGE,"E1.left"),sQuery(id+"F0.wireOp",EDGE,"E1.right")])]});
            var Q1;
            Q1=makeQuery(id+"F3.opExtrude","SWEPT_BODY",BODY,{"disambiguationData":[OSD([sQuery(id+"F2.wireOp",EDGE,"E4.bottom"),sQuery(id+"F2.wireOp",EDGE,"E4.top"),sQuery(id+"F2.wireOp",EDGE,"E4.left"),sQuery(id+"F2.wireOp",EDGE,"E4.right")])]});
            var Q2;
            Q2=makeQuery(id+"F1.opExtrude","SWEPT_BODY",BODY,{"disambiguationData":[OSD([sQuery(id+"F0.wireOp",EDGE,"6c242687-06e7-4fa3-8755-0ec345e10ca5.sketch_text.stroke-45"),sQuery(id+"F0.wireOp",EDGE,"6c242687-06e7-4fa3-8755-0ec345e10ca5.sketch_text.stroke-46"),sQuery(id+"F0.wireOp",EDGE,"6c242687-06e7-4fa3-8755-0ec345e10ca5.sketch_text.stroke-47"),sQuery(id+"F0.wireOp",EDGE,"6c242687-06e7-4fa3-8755-0ec345e10ca5.sketch_text.stroke-48"),sQuery(id+"F0.wireOp",EDGE,"6c242687-06e7-4fa3-8755-0ec345e10ca5.sketch_text.stroke-49"),sQuery(id+"F0.wireOp",EDGE,"6c242687-06e7-4fa3-8755-0ec345e10ca5.sketch_text.stroke-50"),sQuery(id+"F0.wireOp",EDGE,"6c242687-06e7-4fa3-8755-0ec345e10ca5.sketch_text.stroke-51"),sQuery(id+"F0.wireOp",EDGE,"6c242687-06e7-4fa3-8755-0ec345e10ca5.sketch_text.stroke-52")])]});
            var Q3;
            Q3=makeQuery(id+"F1.opExtrude","SWEPT_BODY",BODY,{"disambiguationData":[OSD([sQuery(id+"F0.wireOp",EDGE,"6c242687-06e7-4fa3-8755-0ec345e10ca5.sketch_text.stroke-9"),sQuery(id+"F0.wireOp",EDGE,"6c242687-06e7-4fa3-8755-0ec345e10ca5.sketch_text.stroke-10"),sQuery(id+"F0.wireOp",EDGE,"6c242687-06e7-4fa3-8755-0ec345e10ca5.sketch_text.stroke-11"),sQuery(id+"F0.wireOp",EDGE,"6c242687-06e7-4fa3-8755-0ec345e10ca5.sketch_text.stroke-12"),sQuery(id+"F0.wireOp",EDGE,"6c242687-06e7-4fa3-8755-0ec345e10ca5.sketch_text.stroke-13"),sQuery(id+"F0.wireOp",EDGE,"6c242687-06e7-4fa3-8755-0ec345e10ca5.sketch_text.stroke-14"),sQuery(id+"F0.wireOp",EDGE,"6c242687-06e7-4fa3-8755-0ec345e10ca5.sketch_text.stroke-15"),sQuery(id+"F0.wireOp",EDGE,"6c242687-06e7-4fa3-8755-0ec345e10ca5.sketch_text.stroke-16")])]});
            var Q4;
            Q4=qCreatedBy(makeId("Origin.pointOp"),VERTEX);
            var Q5;
            Q5=qCreatedBy(makeId("Origin.pointOp"),VERTEX);
            transform(context, id + "F14", {"entities" : qUnion([Q0, Q1, Q2, Q3]), "transformType" : TransformType.SCALE_UNIFORMLY, "scale" : .7, "scalePoint" : qUnion([Q5]), "makeCopy" : false});
        }
        {
            var Q0;
            Q0=makeQuery(id+"F8.opLoft","SWEPT_EDGE",EDGE,{"disambiguationData":[OSD([sQuery(id+"F2.wireOp",EDGE,"E4.bottom"),sQuery(id+"F2.wireOp",EDGE,"E4.right")])]});
            var Q1;
            Q1=makeQuery(id+"F8.opLoft","SWEPT_EDGE",EDGE,{"disambiguationData":[OSD([sQuery(id+"F2.wireOp",EDGE,"E4.top"),sQuery(id+"F2.wireOp",EDGE,"E4.left"),sQuery(id+"F2.wireOp",EDGE,"E4.right"),sQuery(id+"F7.wireOp",EDGE,"E5")])]});
            var Q2;
            Q2=makeQuery(id+"F8.opLoft","SWEPT_EDGE",EDGE,{"disambiguationData":[OSD([sQuery(id+"F2.wireOp",EDGE,"E4.bottom"),sQuery(id+"F2.wireOp",EDGE,"E4.top"),sQuery(id+"F2.wireOp",EDGE,"E4.left"),sQuery(id+"F7.wireOp",EDGE,"E5")])]});
            var Q3;
            Q3=makeQuery(id+"F8.opLoft","SWEPT_EDGE",EDGE,{"disambiguationData":[OSD([sQuery(id+"F2.wireOp",EDGE,"E4.bottom"),sQuery(id+"F2.wireOp",EDGE,"E4.left"),sQuery(id+"F2.wireOp",EDGE,"E4.right"),sQuery(id+"F7.wireOp",EDGE,"E5")])]});
            fillet(context, id + "F15", {"entities" : qUnion([Q0, Q1, Q2, Q3]), "radius" : 2.54 * mm, "tangentPropagation" : true, "allowEdgeOverflow" : false});
        }
    });
